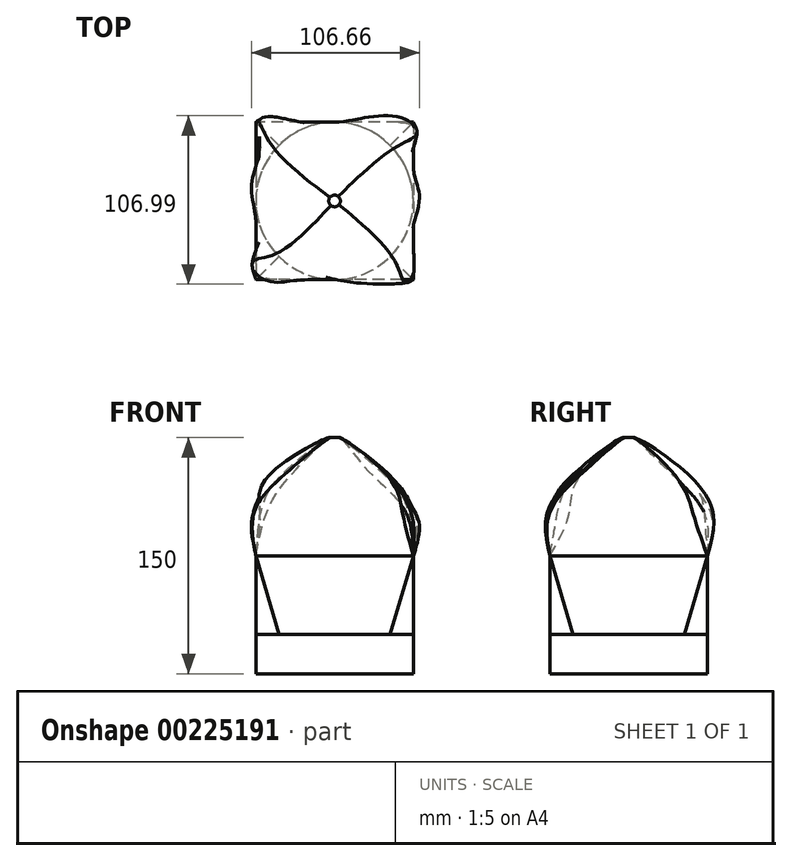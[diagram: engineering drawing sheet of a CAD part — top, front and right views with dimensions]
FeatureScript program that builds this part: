
annotation { "Feature Type Name" : "Feature", "Feature Type Description" : "" }
export const myFeature = defineFeature(function(context is Context, id is Id, definition is map)
    precondition{}
    {
        {
            var Q0;
            Q0=qCreatedBy(makeId("Top.planeOp"),FACE);
            var sketch = newSketch(context, id + "F0", { "sketchPlane" : qUnion([Q0])});
            skCircle(sketch, "E0", {"center": v(0, 0) * mm, "radius": 50 * mm});
            skSolve(sketch);
        }
        {
            var Q0;
            Q0 = qSketchRegion(id + "F0", true);
            extrude(context, id + "F1", {"entities" : qUnion([Q0]), "depth" : 25 * mm});
        }
        {
            var Q0;
            Q0=makeQuery(id+"F1.opExtrude","CAP_FACE",FACE,{"disambiguationData":[OSD([sQuery(id+"F0.wireOp",EDGE,"E0")])],"isStart":false});
            cPlane(context, id + "F2", {"entities" : qUnion([Q0]), "cplaneType" : CPlaneType.OFFSET, "offset" : 50 * mm, "width" : 150 * mm, "height" : 150 * mm});
        }
        {
            var Q0;
            Q0=qCreatedBy(id+"F2.planeOp",FACE);
            var sketch = newSketch(context, id + "F3", { "sketchPlane" : qUnion([Q0])});
            skLineSegment(sketch, "E1.bottom", {"start": v(50, 50) * mm, "end": v(-50, 50) * mm});
            skLineSegment(sketch, "E1.top", {"start": v(50, -50) * mm, "end": v(-50, -50) * mm});
            skLineSegment(sketch, "E1.left", {"start": v(50, 50) * mm, "end": v(50, -50) * mm});
            skLineSegment(sketch, "E1.right", {"start": v(-50, 50) * mm, "end": v(-50, -50) * mm});
            skPoint(sketch, "E1.middle", {"position": v(0, 0) * mm});
            skSolve(sketch);
        }
        {
            var Q0;
            Q0=makeQuery(id+"F1.opExtrude","CAP_FACE",FACE,{"disambiguationData":[OSD([sQuery(id+"F0.wireOp",EDGE,"E0")])],"isStart":false});
            var Q1;
            Q1=makeQuery(id+"F3.imprint","IMPRINT",FACE,{"disambiguationData":[TD([[makeQuery(id+"F3.imprint","IMPRINT",EDGE,{"derivedFrom":sQuery(id+"F3.wireOp",EDGE,"E1.bottom")}),1.0]])]});
            loft(context, id + "F4", {"sheetProfilesArray" : [{ "sheetProfileEntities" : qUnion([Q0]) }, { "sheetProfileEntities" : qUnion([Q1]) }]});
        }
        {
            var Q0;
            Q0=makeQuery(id+"F4.opLoft","CAP_FACE",FACE,{"disambiguationData":[OSD([makeQuery(id+"F3.imprint","IMPRINT",FACE,{"disambiguationData":[TD([[makeQuery(id+"F3.imprint","IMPRINT",EDGE,{"derivedFrom":sQuery(id+"F3.wireOp",EDGE,"E1.bottom")}),1.0]])]})])],"isStart":true});
            cPlane(context, id + "F5", {"entities" : qUnion([Q0]), "cplaneType" : CPlaneType.OFFSET, "offset" : 25 * mm, "width" : 150 * mm, "height" : 150 * mm});
        }
        {
            var Q0;
            Q0=qCreatedBy(id+"F5.planeOp",FACE);
            var sketch = newSketch(context, id + "F6", { "sketchPlane" : qUnion([Q0])});
            skFitSpline(sketch, "E2", {"points": [v(0, -49.3) * mm, v(-20.08, -45.84) * mm, v(-37, -51.19) * mm, v(-51.45, -42.1) * mm, v(-44.67, -20.18) * mm, v(-44.85, -14.83) * mm, v(-52.16, 10.12) * mm, v(-47.52, 30.26) * mm, v(-47.88, 42.91) * mm, v(-44.5, 52.18) * mm, v(-11.35, 48.26) * mm, v(19.66, 52.9) * mm, v(44.43, 51.64) * mm, v(51.56, 41.3) * mm, v(47.1, 21.88) * mm, v(52.45, 2.81) * mm, v(46.4, -23.2) * mm, v(49.07, -46.37) * mm, v(37.48, -51.9) * mm, v(0, -49.3) * mm]});
            skSolve(sketch);
        }
        {
            var Q0;
            Q0=qCreatedBy(id+"F5.planeOp",FACE);
            cPlane(context, id + "F7", {"entities" : qUnion([Q0]), "cplaneType" : CPlaneType.OFFSET, "offset" : 25 * mm, "width" : 150 * mm, "height" : 150 * mm});
        }
        {
            var Q0;
            Q0=qCreatedBy(id+"F7.planeOp",FACE);
            var sketch = newSketch(context, id + "F8", { "sketchPlane" : qUnion([Q0])});
            skFitSpline(sketch, "E3", {"points": [v(-33.27, -34.92) * mm, v(-29.07, -5.84) * mm, v(-42.56, 20.53) * mm, v(-20.08, 36.12) * mm, v(5.7, 39.11) * mm, v(35.97, 26.23) * mm, v(25.18, -4.05) * mm, v(34.47, -31.62) * mm, v(-9.3, -34.92) * mm, v(-33.27, -34.92) * mm]});
            skSolve(sketch);
        }
        {
            var Q0;
            Q0=qCreatedBy(id+"F7.planeOp",FACE);
            cPlane(context, id + "F9", {"entities" : qUnion([Q0]), "cplaneType" : CPlaneType.OFFSET, "offset" : 25 * mm, "width" : 150 * mm, "height" : 150 * mm});
        }
        {
            var Q0;
            Q0=qCreatedBy(id+"F9.planeOp",FACE);
            var sketch = newSketch(context, id + "F10", { "sketchPlane" : qUnion([Q0])});
            skCircle(sketch, "E4", {"center": v(0, 0) * mm, "radius": 3.71 * mm});
            skLineSegment(sketch, "E5", {"start": v(0, 0) * mm, "end": v(0, 35.28) * mm, "construction": true});
            skSolve(sketch);
        }
        {
            var Q1;
            Q1=makeQuery(id+"F4.opLoft","CAP_FACE",FACE,{"disambiguationData":[OSD([makeQuery(id+"F3.imprint","IMPRINT",FACE,{"disambiguationData":[TD([[makeQuery(id+"F3.imprint","IMPRINT",EDGE,{"derivedFrom":sQuery(id+"F3.wireOp",EDGE,"E1.bottom")}),1.0]])]})])],"isStart":true});
            var Q2;
            Q2=makeQuery(id+"F6.imprint","IMPRINT",FACE,{"disambiguationData":[TD([[makeQuery(id+"F6.imprint","IMPRINT",EDGE,{"derivedFrom":sQuery(id+"F6.wireOp",EDGE,"E2")}),-1.0]])]});
            var Q3;
            Q3=makeQuery(id+"F8.imprint","IMPRINT",FACE,{"disambiguationData":[TD([[makeQuery(id+"F8.imprint","IMPRINT",EDGE,{"derivedFrom":sQuery(id+"F8.wireOp",EDGE,"E3")}),-1.0]])]});
            var Q4;
            Q4=makeQuery(id+"F10.imprint","IMPRINT",FACE,{"disambiguationData":[TD([[makeQuery(id+"F10.imprint","IMPRINT",EDGE,{"derivedFrom":sQuery(id+"F10.wireOp",EDGE,"E4")}),1.0]])]});
            loft(context, id + "F11", {"operationType" : NewBodyOperationType.ADD, "endCondition" : LoftEndDerivativeType.TANGENT_TO_PROFILE, "endMagnitude" : 0.2, "sheetProfilesArray" : [{ "sheetProfileEntities" : qUnion([Q1]) }, { "sheetProfileEntities" : qUnion([Q2]) }, { "sheetProfileEntities" : qUnion([Q3]) }, { "sheetProfileEntities" : qUnion([Q4]) }]});
        }
    });
